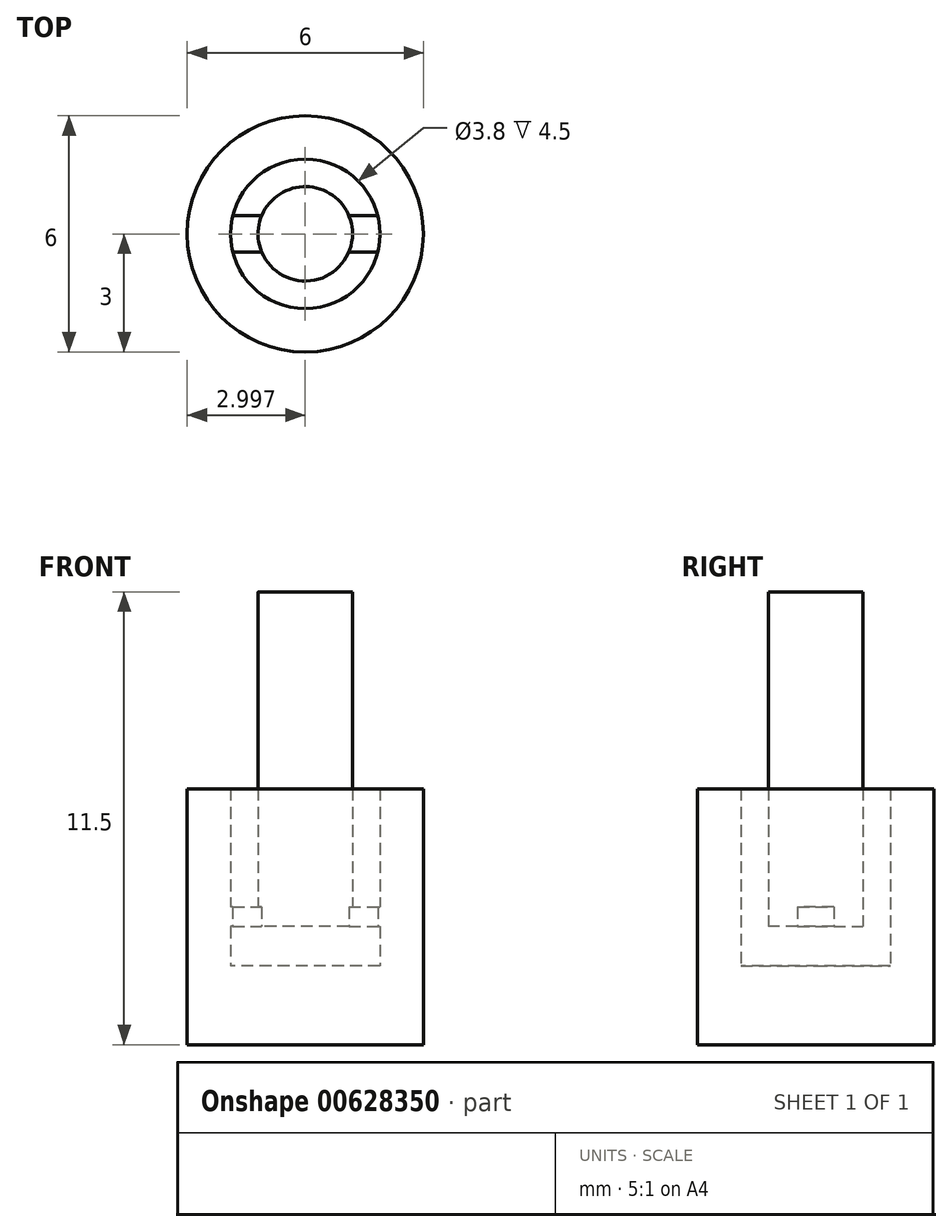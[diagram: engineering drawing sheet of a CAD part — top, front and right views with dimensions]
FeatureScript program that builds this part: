
annotation { "Feature Type Name" : "Feature", "Feature Type Description" : "" }
export const myFeature = defineFeature(function(context is Context, id is Id, definition is map)
    precondition{}
    {
        {
            var Q0;
            Q0=qCreatedBy(makeId("Top.planeOp"),FACE);
            var sketch = newSketch(context, id + "F0", { "sketchPlane" : qUnion([Q0])});
            skCircle(sketch, "E0", {"center": v(-10.44, 0) * mm, "radius": 3 * mm});
            skCircle(sketch, "E1", {"center": v(-10.44, 0) * mm, "radius": 1.9 * mm});
            skCircle(sketch, "E2", {"center": v(-10.44, 0) * mm, "radius": 1.2 * mm});
            skSolve(sketch);
        }
        {
            var Q0;
            Q0=makeQuery(id+"F0.imprint","IMPRINT",FACE,{"disambiguationData":[TD([[makeQuery(id+"F0.imprint","IMPRINT",EDGE,{"derivedFrom":sQuery(id+"F0.wireOp",EDGE,"E0")}),1.0]])]});
            var Q1;
            Q1=makeQuery(id+"F0.imprint","IMPRINT",FACE,{"disambiguationData":[TD([[makeQuery(id+"F0.imprint","IMPRINT",EDGE,{"derivedFrom":sQuery(id+"F0.wireOp",EDGE,"E1")}),1.0]])]});
            var Q2;
            Q2=makeQuery(id+"F0.imprint","IMPRINT",FACE,{"disambiguationData":[TD([[makeQuery(id+"F0.imprint","IMPRINT",EDGE,{"derivedFrom":sQuery(id+"F0.wireOp",EDGE,"E2")}),1.0]])]});
            var Q3;
            Q3=sQuery(id+"F0.wireOp",EDGE,"E0");
            extrude(context, id + "F1", {"entities" : qUnion([Q0, Q1, Q2]), "surfaceEntities" : qUnion([Q3]), "depth" : 2 * mm, "offsetDistance" : 25 * mm});
        }
        {
            var Q0;
            Q0=makeQuery(id+"F1.opExtrude","CAP_FACE",FACE,{"disambiguationData":[OSD([sQuery(id+"F0.wireOp",EDGE,"E0")])],"isStart":false});
            var sketch = newSketch(context, id + "F2", { "sketchPlane" : qUnion([Q0])});
            skCircle(sketch, "E3", {"center": v(-10.44, 0) * mm, "radius": 3 * mm});
            skCircle(sketch, "E4", {"center": v(-10.44, 0) * mm, "radius": 1.9 * mm});
            skSolve(sketch);
        }
        {
            var Q0;
            Q0=makeQuery(id+"F2.imprint","IMPRINT",FACE,{"disambiguationData":[TD([[makeQuery(id+"F2.imprint","IMPRINT",EDGE,{"derivedFrom":sQuery(id+"F2.wireOp",EDGE,"E3")}),1.0]])]});
            extrude(context, id + "F3", {"entities" : qUnion([Q0]), "operationType" : NewBodyOperationType.ADD, "depth" : 1 * mm, "offsetDistance" : 25 * mm});
        }
        {
            var Q0;
            Q0=makeQuery(id+"F3.opExtrude","CAP_FACE",FACE,{"disambiguationData":[OSD([sQuery(id+"F2.wireOp",EDGE,"E3"),sQuery(id+"F2.wireOp",EDGE,"E4")])],"isStart":false});
            var sketch = newSketch(context, id + "F4", { "sketchPlane" : qUnion([Q0])});
            skCircle(sketch, "E5", {"center": v(-10.44, 0) * mm, "radius": 1.2 * mm});
            skCircle(sketch, "E6", {"center": v(-10.44, 0) * mm, "radius": 1.9 * mm});
            skCircle(sketch, "E7", {"center": v(-10.44, 0) * mm, "radius": 3 * mm});
            skLineSegment(sketch, "E8.bottom", {"start": v(-12.76, 0.46) * mm, "end": v(-7.88, 0.46) * mm});
            skLineSegment(sketch, "E8.top", {"start": v(-12.76, -0.46) * mm, "end": v(-7.88, -0.46) * mm});
            skLineSegment(sketch, "E8.left", {"start": v(-12.76, 0.46) * mm, "end": v(-12.76, -0.46) * mm});
            skLineSegment(sketch, "E8.right", {"start": v(-7.88, 0.46) * mm, "end": v(-7.88, -0.46) * mm});
            skPoint(sketch, "E9", {"position": v(-7.88, 0) * mm});
            skSolve(sketch);
        }
        {
            var Q0;
            Q0=makeQuery(id+"F4.imprint","IMPRINT",FACE,{"disambiguationData":[TD([[makeQuery(id+"F4.imprint","IMPRINT",EDGE,{"derivedFrom":sQuery(id+"F4.wireOp",EDGE,"E7")}),1.0]])]});
            var Q1;
            {var subQ5=sQuery(id+"F4.wireOp",EDGE,"E8.left");Q1=makeQuery(id+"F4.imprint","IMPRINT",FACE,{"disambiguationData":[TD([[makeQuery(id+"F4.imprint","IMPRINT",EDGE,{"derivedFrom":subQ5}),1.0]])]});}
            var Q2;
            {var subQ0=sQuery(id+"F4.wireOp",EDGE,"E8.bottom");var subQ1=sQuery(id+"F4.wireOp",EDGE,"E5");var subQ2=makeQuery(id+"F4.imprint","INTERSECT",VERTEX,{"disambiguationData":[OD(0.0)],"derivedFrom":[subQ1,subQ0]});Q2=makeQuery(id+"F4.imprint","IMPRINT",FACE,{"disambiguationData":[TD([[makeQuery(id+"F4.imprint","IMPRINT",EDGE,{"disambiguationData":[TD([[subQ2,-1.0]])],"derivedFrom":subQ1}),-1.0]])]});}
            var Q3;
            {var subQ0=sQuery(id+"F4.wireOp",EDGE,"E8.bottom");var subQ1=sQuery(id+"F4.wireOp",EDGE,"E5");var subQ2=makeQuery(id+"F4.imprint","INTERSECT",VERTEX,{"disambiguationData":[OD(0.0)],"derivedFrom":[subQ1,subQ0]});Q3=makeQuery(id+"F4.imprint","IMPRINT",FACE,{"disambiguationData":[TD([[makeQuery(id+"F4.imprint","IMPRINT",EDGE,{"disambiguationData":[TD([[subQ2,-1.0]])],"derivedFrom":subQ1}),1.0]])]});}
            var Q4;
            {var subQ0=sQuery(id+"F4.wireOp",EDGE,"E8.bottom");var subQ1=sQuery(id+"F4.wireOp",EDGE,"E5");var subQ2=makeQuery(id+"F4.imprint","INTERSECT",VERTEX,{"disambiguationData":[OD(0.0)],"derivedFrom":[subQ1,subQ0]});Q4=makeQuery(id+"F4.imprint","IMPRINT",FACE,{"disambiguationData":[TD([[makeQuery(id+"F4.imprint","IMPRINT",EDGE,{"disambiguationData":[TD([[subQ2,1.0]])],"derivedFrom":subQ1}),1.0]])]});}
            var Q5;
            {var subQ0=sQuery(id+"F4.wireOp",EDGE,"E8.top");var subQ1=sQuery(id+"F4.wireOp",EDGE,"E5");var subQ2=makeQuery(id+"F4.imprint","INTERSECT",VERTEX,{"disambiguationData":[OD(0.0)],"derivedFrom":[subQ1,subQ0]});Q5=makeQuery(id+"F4.imprint","IMPRINT",FACE,{"disambiguationData":[TD([[makeQuery(id+"F4.imprint","IMPRINT",EDGE,{"disambiguationData":[TD([[subQ2,-1.0]])],"derivedFrom":subQ1}),1.0]])]});}
            var Q6;
            {var subQ0=sQuery(id+"F4.wireOp",EDGE,"E8.bottom");var subQ1=sQuery(id+"F4.wireOp",EDGE,"E5");var subQ2=makeQuery(id+"F4.imprint","INTERSECT",VERTEX,{"disambiguationData":[OD(1.0)],"derivedFrom":[subQ1,subQ0]});Q6=makeQuery(id+"F4.imprint","IMPRINT",FACE,{"disambiguationData":[TD([[makeQuery(id+"F4.imprint","IMPRINT",EDGE,{"disambiguationData":[TD([[subQ2,1.0]])],"derivedFrom":subQ1}),-1.0]])]});}
            var Q7;
            {var subQ5=sQuery(id+"F4.wireOp",EDGE,"E8.right");Q7=makeQuery(id+"F4.imprint","IMPRINT",FACE,{"disambiguationData":[TD([[makeQuery(id+"F4.imprint","IMPRINT",EDGE,{"derivedFrom":subQ5}),-1.0]])]});}
            extrude(context, id + "F5", {"entities" : qUnion([Q0, Q1, Q2, Q3, Q4, Q5, Q6, Q7]), "operationType" : NewBodyOperationType.ADD, "depth" : .5 * mm, "offsetDistance" : 25 * mm});
        }
        {
            var Q0;
            Q0=makeQuery(id+"F5.opExtrude","CAP_FACE",FACE,{"disambiguationData":[OSD([sQuery(id+"F4.wireOp",EDGE,"E5"),sQuery(id+"F4.wireOp",EDGE,"E6"),sQuery(id+"F4.wireOp",EDGE,"E7"),sQuery(id+"F4.wireOp",EDGE,"E8.bottom"),sQuery(id+"F4.wireOp",EDGE,"E8.top")])],"isStart":false});
            var sketch = newSketch(context, id + "F6", { "sketchPlane" : qUnion([Q0])});
            skCircle(sketch, "E10", {"center": v(-10.44, 0) * mm, "radius": 1.2 * mm});
            skCircle(sketch, "E11", {"center": v(-10.44, 0) * mm, "radius": 1.9 * mm});
            skCircle(sketch, "E12", {"center": v(-10.44, 0) * mm, "radius": 3 * mm});
            skSolve(sketch);
        }
        {
            var Q0;
            Q0=makeQuery(id+"F6.imprint","IMPRINT",FACE,{"disambiguationData":[TD([[makeQuery(id+"F6.imprint","IMPRINT",EDGE,{"derivedFrom":sQuery(id+"F6.wireOp",EDGE,"E12")}),1.0]])]});
            var Q1;
            {var subQ0=sQuery(id+"F6.wireOp",EDGE,"E10");var subQ1=sQuery(id+"F4.wireOp",EDGE,"E8.bottom");var subQ2=sQuery(id+"F4.wireOp",EDGE,"E5");var subQ4=makeQuery(id+"F6.imprint","INTERSECT",VERTEX,{"derivedFrom":[makeQuery(id+"F5.opExtrude","CAP_EDGE",EDGE,{"disambiguationData":[OSD([subQ1]),TDD([makeQuery(id+"F4.imprint","IMPRINT",EDGE,{"disambiguationData":[TD([[makeQuery(id+"F4.imprint","INTERSECT",VERTEX,{"disambiguationData":[OD(0.0)],"derivedFrom":[subQ2,subQ1]}),1.0]])],"derivedFrom":subQ1})])],"isStart":false}),subQ0]});Q1=makeQuery(id+"F6.imprint","IMPRINT",FACE,{"disambiguationData":[TD([[makeQuery(id+"F6.imprint","IMPRINT",EDGE,{"disambiguationData":[TD([[subQ4,1.0]])],"derivedFrom":subQ0}),1.0]])]});}
            extrude(context, id + "F7", {"entities" : qUnion([Q0, Q1]), "operationType" : NewBodyOperationType.ADD, "depth" : 3 * mm, "offsetDistance" : 25 * mm});
        }
        {
            var Q0;
            Q0=makeQuery(id+"F7.opExtrude","CAP_FACE",FACE,{"disambiguationData":[OSD([sQuery(id+"F6.wireOp",EDGE,"E10")])],"isStart":false});
            extrude(context, id + "F8", {"entities" : qUnion([Q0]), "operationType" : NewBodyOperationType.ADD, "depth" : 5 * mm, "offsetDistance" : 25 * mm});
        }
    });
